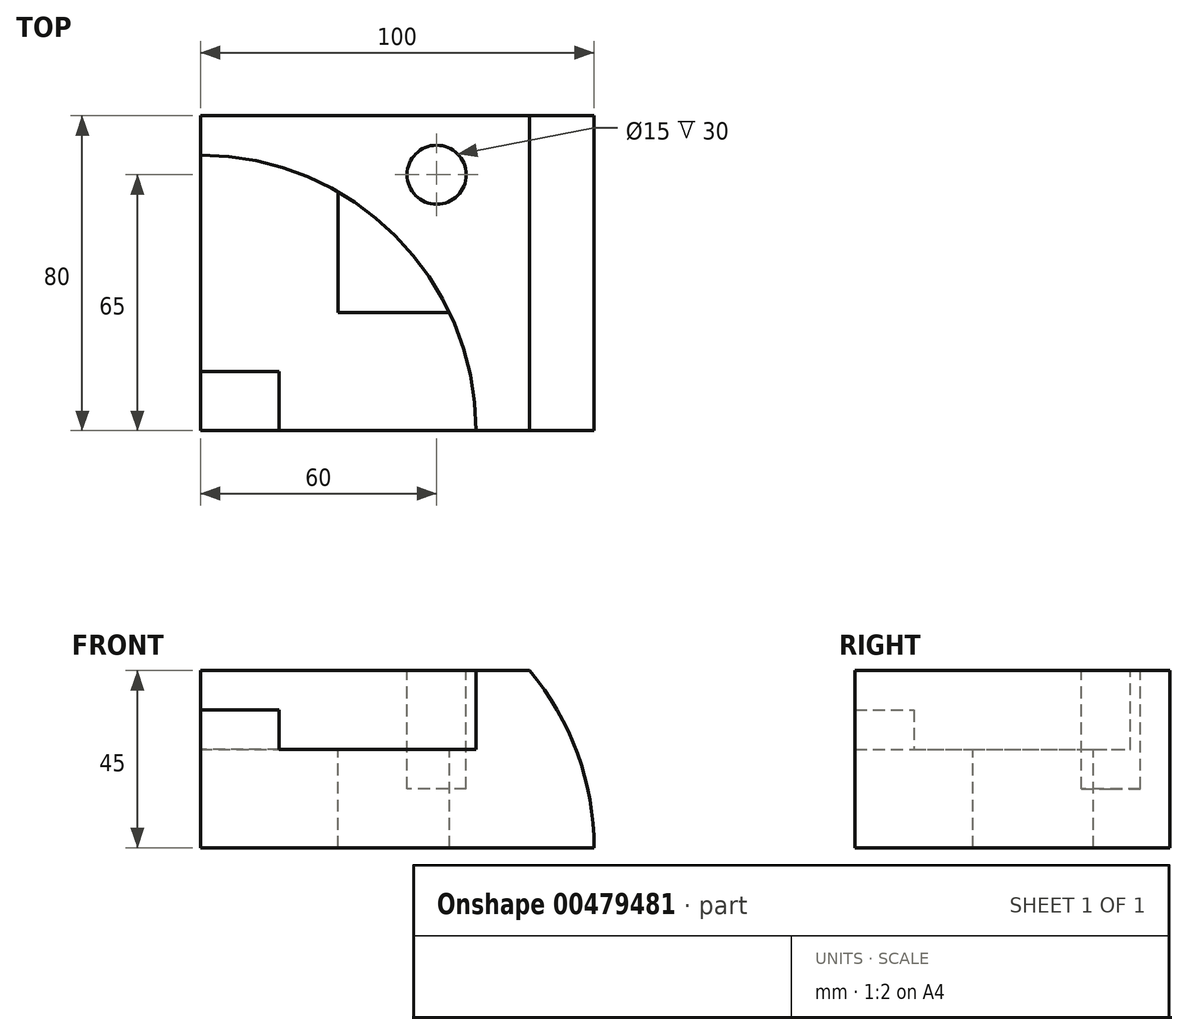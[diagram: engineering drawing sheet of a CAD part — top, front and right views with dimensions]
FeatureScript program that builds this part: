
annotation { "Feature Type Name" : "Feature", "Feature Type Description" : "" }
export const myFeature = defineFeature(function(context is Context, id is Id, definition is map)
    precondition{}
    {
        {
            var Q0;
            Q0=qCreatedBy(makeId("Top.planeOp"),FACE);
            var sketch = newSketch(context, id + "F0", { "sketchPlane" : qUnion([Q0])});
            skLineSegment(sketch, "E0.bottom", {"start": v(0, 0) * mm, "end": v(100, 0) * mm});
            skLineSegment(sketch, "E0.top", {"start": v(0, 80) * mm, "end": v(100, 80) * mm});
            skLineSegment(sketch, "E0.left", {"start": v(0, 0) * mm, "end": v(0, 80) * mm});
            skLineSegment(sketch, "E0.right", {"start": v(100, 0) * mm, "end": v(100, 80) * mm});
            skSolve(sketch);
        }
        {
            var Q0;
            Q0 = qSketchRegion(id + "F0", true);
            extrude(context, id + "F1", {"entities" : qUnion([Q0]), "depth" : 45 * mm});
        }
        {
            var Q0;
            Q0=makeQuery(id+"F1.opExtrude","CAP_FACE",FACE,{"disambiguationData":[OSD([sQuery(id+"F0.wireOp",EDGE,"E0.bottom"),sQuery(id+"F0.wireOp",EDGE,"E0.top"),sQuery(id+"F0.wireOp",EDGE,"E0.left"),sQuery(id+"F0.wireOp",EDGE,"E0.right")])],"isStart":false});
            var sketch = newSketch(context, id + "F2", { "sketchPlane" : qUnion([Q0])});
            skCircle(sketch, "E1", {"center": v(0, 0) * mm, "radius": 70 * mm});
            skSolve(sketch);
        }
        {
            var Q0;
            {var subQ0=sQuery(id+"F2.wireOp",EDGE,"E1");var subQ1=makeQuery(id+"F1.opExtrude","CAP_EDGE",EDGE,{"disambiguationData":[OSD([sQuery(id+"F0.wireOp",EDGE,"E0.bottom")])],"isStart":false});var subQ2=makeQuery(id+"F2.imprint","INTERSECT",VERTEX,{"derivedFrom":[subQ1,subQ0]});Q0=makeQuery(id+"F2.imprint","IMPRINT",FACE,{"disambiguationData":[TD([[makeQuery(id+"F2.imprint","IMPRINT",EDGE,{"disambiguationData":[TD([[subQ2,-1.0]])],"derivedFrom":subQ0}),1.0]])]});}
            extrude(context, id + "F3", {"entities" : qUnion([Q0]), "operationType" : NewBodyOperationType.REMOVE, "oppositeDirection" : true, "depth" : 20 * mm});
        }
        {
            var Q0;
            Q0=makeQuery(id+"F3.boolean.opBoolean","COPY",FACE,{"derivedFrom":makeQuery(id+"F3.opExtrude","CAP_FACE",FACE,{"disambiguationData":[OSD([sQuery(id+"F0.wireOp",EDGE,"E0.bottom"),sQuery(id+"F0.wireOp",EDGE,"E0.left"),sQuery(id+"F2.wireOp",EDGE,"E1")])],"isStart":false})});
            var sketch = newSketch(context, id + "F4", { "sketchPlane" : qUnion([Q0])});
            skLineSegment(sketch, "E2.bottom", {"start": v(0, 0) * mm, "end": v(20, 0) * mm});
            skLineSegment(sketch, "E2.top", {"start": v(0, 15) * mm, "end": v(20, 15) * mm});
            skLineSegment(sketch, "E2.left", {"start": v(0, 0) * mm, "end": v(0, 15) * mm});
            skLineSegment(sketch, "E2.right", {"start": v(20, 0) * mm, "end": v(20, 15) * mm});
            skSolve(sketch);
        }
        {
            var Q0;
            Q0 = qSketchRegion(id + "F4", true);
            extrude(context, id + "F5", {"entities" : qUnion([Q0]), "operationType" : NewBodyOperationType.ADD, "depth" : 10 * mm});
        }
        {
            var Q0;
            Q0=makeQuery(id+"F3.boolean.opBoolean","COPY",FACE,{"derivedFrom":makeQuery(id+"F3.opExtrude","CAP_FACE",FACE,{"disambiguationData":[OSD([sQuery(id+"F0.wireOp",EDGE,"E0.bottom"),sQuery(id+"F0.wireOp",EDGE,"E0.left"),sQuery(id+"F2.wireOp",EDGE,"E1")])],"isStart":false})});
            var sketch = newSketch(context, id + "F6", { "sketchPlane" : qUnion([Q0])});
            skLineSegment(sketch, "E3.bottom", {"start": v(35, 30) * mm, "end": v(76.7, 30) * mm});
            skLineSegment(sketch, "E3.top", {"start": v(35, 71.79) * mm, "end": v(76.7, 71.79) * mm});
            skLineSegment(sketch, "E3.left", {"start": v(35, 30) * mm, "end": v(35, 71.79) * mm});
            skLineSegment(sketch, "E3.right", {"start": v(76.7, 30) * mm, "end": v(76.7, 71.79) * mm});
            skSolve(sketch);
        }
        {
            var Q0;
            {var subQ0=sQuery(id+"F6.wireOp",EDGE,"E3.left");var subQ1=sQuery(id+"F6.wireOp",EDGE,"E3.bottom");var subQ2=makeQuery(id+"F6.imprint","INTERSECT",VERTEX,{"derivedFrom":[subQ1,subQ0]});Q0=makeQuery(id+"F6.imprint","IMPRINT",FACE,{"disambiguationData":[TD([[makeQuery(id+"F6.imprint","IMPRINT",EDGE,{"disambiguationData":[TD([[subQ2,-1.0]])],"derivedFrom":subQ1}),1.0]])]});}
            extrude(context, id + "F7", {"entities" : qUnion([Q0]), "operationType" : NewBodyOperationType.REMOVE, "endBound" : BoundingType.THROUGH_ALL, "oppositeDirection" : true, "depth" : 25 * mm});
        }
        {
            var Q0;
            Q0=makeQuery(id+"F1.opExtrude","CAP_FACE",FACE,{"disambiguationData":[OSD([sQuery(id+"F0.wireOp",EDGE,"E0.bottom"),sQuery(id+"F0.wireOp",EDGE,"E0.top"),sQuery(id+"F0.wireOp",EDGE,"E0.left"),sQuery(id+"F0.wireOp",EDGE,"E0.right")])],"isStart":false});
            var sketch = newSketch(context, id + "F8", { "sketchPlane" : qUnion([Q0])});
            skCircle(sketch, "E4", {"center": v(60, 65) * mm, "radius": 7.5 * mm});
            skSolve(sketch);
        }
        {
            var Q0;
            Q0 = qSketchRegion(id + "F8", true);
            extrude(context, id + "F9", {"entities" : qUnion([Q0]), "operationType" : NewBodyOperationType.REMOVE, "oppositeDirection" : true, "depth" : 30 * mm});
        }
        {
            var Q0;
            Q0=makeQuery(id+"F5.boolean.opBoolean","MERGE",FACE,{"derivedFrom":[makeQuery(id+"F1.opExtrude","SWEPT_FACE",FACE,{"disambiguationData":[OSD([sQuery(id+"F0.wireOp",EDGE,"E0.bottom")])]}),makeQuery(id+"F5.opExtrude","SWEPT_FACE",FACE,{"disambiguationData":[OSD([sQuery(id+"F4.wireOp",EDGE,"E2.bottom")])]})]});
            var sketch = newSketch(context, id + "F10", { "sketchPlane" : qUnion([Q0])});
            skArc(sketch, "E5", {"start": v(100, 0) * mm, "mid": v(95.78, 23.94) * mm, "end": v(83.62, 45) * mm});
            skSolve(sketch);
        }
        {
            var Q0;
            {var subQ0=sQuery(id+"F10.wireOp",EDGE,"E5");Q0=makeQuery(id+"F10.imprint","IMPRINT",FACE,{"disambiguationData":[TD([[makeQuery(id+"F10.imprint","IMPRINT",EDGE,{"derivedFrom":subQ0}),-1.0]])]});}
            extrude(context, id + "F11", {"entities" : qUnion([Q0]), "operationType" : NewBodyOperationType.REMOVE, "endBound" : BoundingType.THROUGH_ALL, "oppositeDirection" : true, "depth" : 25 * mm});
        }
    });
